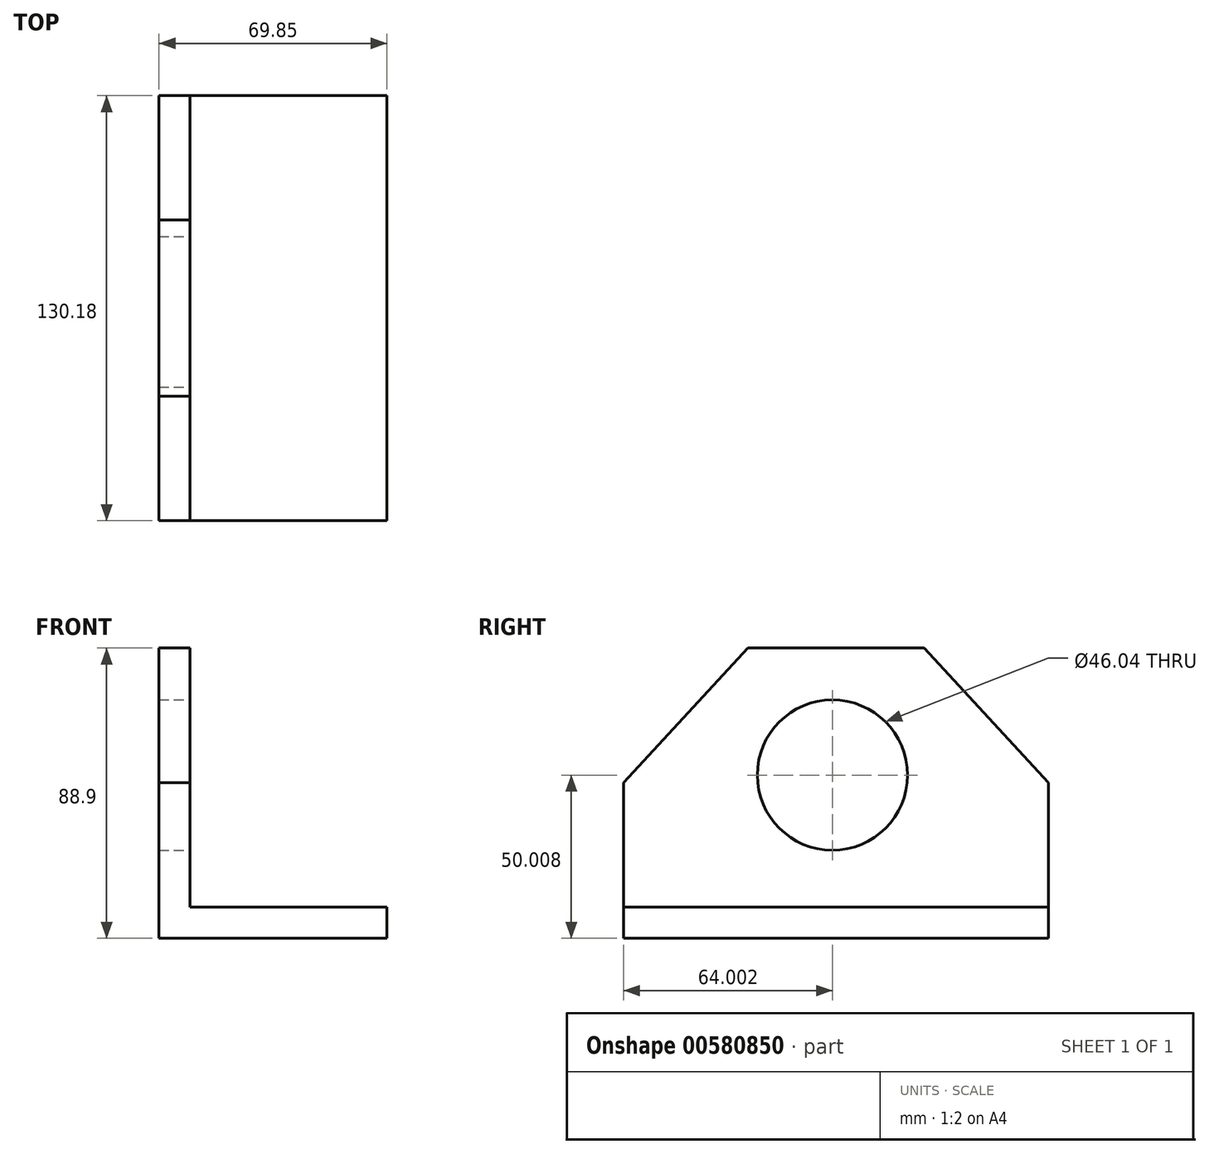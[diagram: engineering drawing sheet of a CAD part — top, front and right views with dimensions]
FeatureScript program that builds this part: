
annotation { "Feature Type Name" : "Feature", "Feature Type Description" : "" }
export const myFeature = defineFeature(function(context is Context, id is Id, definition is map)
    precondition{}
    {
        {
            var Q0;
            Q0=qCreatedBy(makeId("Front.planeOp"),FACE);
            var sketch = newSketch(context, id + "F0", { "sketchPlane" : qUnion([Q0])});
            skLineSegment(sketch, "E0.bottom", {"start": v(-47.66, 38.68) * mm, "end": v(-38.13, 38.68) * mm});
            skLineSegment(sketch, "E0.top", {"start": v(-47.66, -50.22) * mm, "end": v(22.2, -50.22) * mm});
            skLineSegment(sketch, "E0.left", {"start": v(-47.66, 38.68) * mm, "end": v(-47.66, -50.22) * mm});
            skLineSegment(sketch, "E0.right", {"start": v(22.2, -40.7) * mm, "end": v(22.2, -50.22) * mm});
            skLineSegment(sketch, "E1.top", {"start": v(22.2, -40.7) * mm, "end": v(-38.13, -40.7) * mm});
            skLineSegment(sketch, "E1.right", {"start": v(-38.13, 38.68) * mm, "end": v(-38.13, -40.7) * mm});
            skSolve(sketch);
        }
        {
            var Q0;
            Q0 = qSketchRegion(id + "F0", true);
            extrude(context, id + "F1", {"entities" : qUnion([Q0]), "depth" : 130.17 * mm, "offsetDistance" : 25.4 * mm});
        }
        {
            var Q0;
            Q0=makeQuery(id+"F1.opExtrude","SWEPT_FACE",FACE,{"disambiguationData":[OSD([sQuery(id+"F0.wireOp",EDGE,"E1.right")])]});
            var sketch = newSketch(context, id + "F2", { "sketchPlane" : qUnion([Q0])});
            skLineSegment(sketch, "E2", {"start": v(-92.08, 38.68) * mm, "end": v(-130.18, -2.6) * mm});
            skLineSegment(sketch, "E3", {"start": v(0, -2.6) * mm, "end": v(-38.1, 38.68) * mm});
            skLineSegment(sketch, "E4", {"start": v(-130.18, -2.6) * mm, "end": v(-130.18, 38.68) * mm});
            skLineSegment(sketch, "E5", {"start": v(-130.18, 38.68) * mm, "end": v(-92.08, 38.68) * mm});
            skLineSegment(sketch, "E6", {"start": v(0, 38.68) * mm, "end": v(0, 0) * mm});
            skLineSegment(sketch, "E7", {"start": v(0, 0) * mm, "end": v(0, -2.6) * mm});
            skLineSegment(sketch, "E8.trimOffspring", {"start": v(-38.1, 38.68) * mm, "end": v(0, 38.68) * mm});
            skCircle(sketch, "E9", {"center": v(-66.18, -0.21) * mm, "radius": 23.02 * mm});
            skSolve(sketch);
        }
        {
            var Q0;
            Q0 = qSketchRegion(id + "F2", true);
            extrude(context, id + "F3", {"entities" : qUnion([Q0]), "operationType" : NewBodyOperationType.REMOVE, "oppositeDirection" : true, "depth" : 25.4 * mm, "offsetDistance" : 25.4 * mm});
        }
    });
